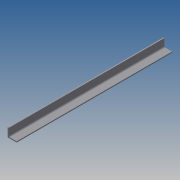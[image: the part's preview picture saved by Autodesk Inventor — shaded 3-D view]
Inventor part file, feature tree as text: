
AUTODESK INVENTOR PART (.ipt)
format: ipt  version: 2014 SP1 (Build 180222100, 222)  size: 76,800 bytes
history: native  units: in
note: dims shown in document units (in); Inventor stores cm internally (conversion verified against a paired STEP export)
features: extrude x1, sketch x1
ambient origin geometry x8: Origin, YZ Plane, XZ Plane, XY Plane, X Axis, Y Axis, Z Axis, Center Point
bodies: Solid1 (feature_tree)
feature tree (2):
  extrude  "Extrusion1"  Depth=1.0in
  sketch  "Sketch1"  dims[d0=1.0in d1=1.0in d2=0.1181in d3=0.1476in d4=17.6181in d5=0.0in]
